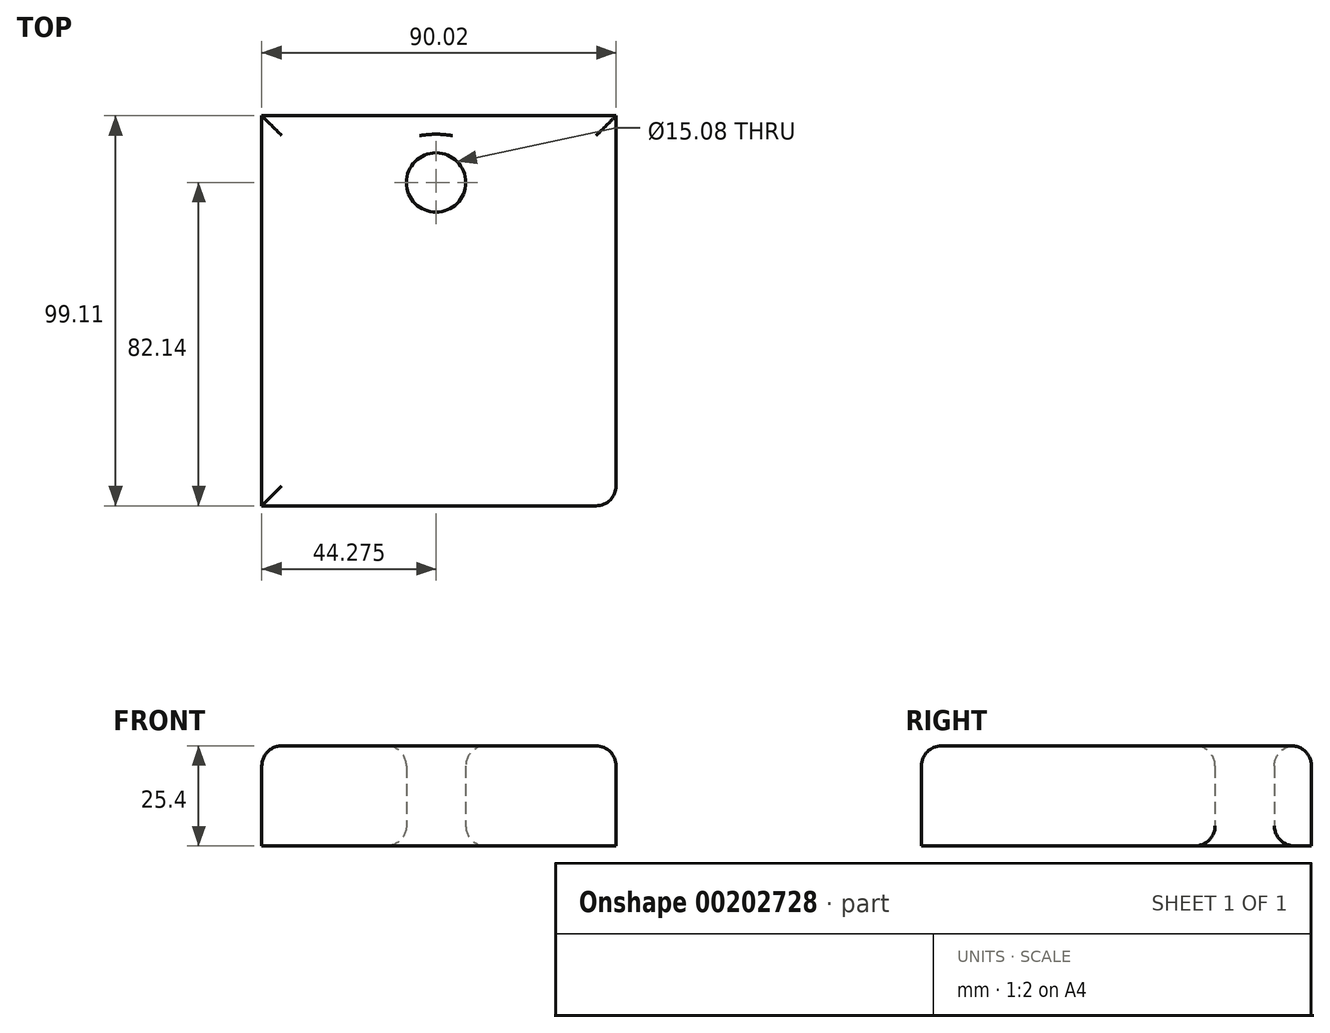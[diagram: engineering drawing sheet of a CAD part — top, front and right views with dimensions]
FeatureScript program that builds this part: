
annotation { "Feature Type Name" : "Feature", "Feature Type Description" : "" }
export const myFeature = defineFeature(function(context is Context, id is Id, definition is map)
    precondition{}
    {
        {
            var Q0;
            Q0=qCreatedBy(makeId("Top.planeOp"),FACE);
            var sketch = newSketch(context, id + "F0", { "sketchPlane" : qUnion([Q0])});
            skLineSegment(sketch, "E0.bottom", {"start": v(-44.12, 51.7) * mm, "end": v(45.9, 51.7) * mm});
            skLineSegment(sketch, "E0.top", {"start": v(-44.12, -47.41) * mm, "end": v(45.9, -47.41) * mm});
            skLineSegment(sketch, "E0.left", {"start": v(-44.12, 51.7) * mm, "end": v(-44.12, -47.41) * mm});
            skLineSegment(sketch, "E0.right", {"start": v(45.9, 51.7) * mm, "end": v(45.9, -47.41) * mm});
            skLineSegment(sketch, "E1", {"start": v(0, 51.7) * mm, "end": v(0.89, -45.83) * mm});
            skPoint(sketch, "E1.endSnap0", {"position": v(0.89, -47.41) * mm});
            skLineSegment(sketch, "E2", {"start": v(0.89, -45.83) * mm, "end": v(0.89, -47.41) * mm});
            skCircle(sketch, "E3", {"center": v(0.15, 34.73) * mm, "radius": 7.54 * mm});
            skSolve(sketch);
        }
        {
            var Q0;
            Q0 = qSketchRegion(id + "F0", true);
            extrude(context, id + "F1", {"entities" : qUnion([Q0]), "depth" : 25.4 * mm});
        }
        {
            var Q0;
            Q0=makeQuery(id+"F1.opExtrude","CAP_EDGE",EDGE,{"disambiguationData":[OSD([sQuery(id+"F0.wireOp",EDGE,"E0.top")])],"isStart":false});
            var Q1;
            Q1=makeQuery(id+"F1.opExtrude","CAP_EDGE",EDGE,{"disambiguationData":[OSD([sQuery(id+"F0.wireOp",EDGE,"E0.right")])],"isStart":false});
            var Q2;
            Q2=makeQuery(id+"F1.opExtrude","SWEPT_EDGE",EDGE,{"disambiguationData":[OSD([sQuery(id+"F0.wireOp",EDGE,"E0.top"),sQuery(id+"F0.wireOp",EDGE,"E0.right")])]});
            var Q3;
            Q3=makeQuery(id+"F1.opExtrude","CAP_EDGE",EDGE,{"disambiguationData":[OSD([sQuery(id+"F0.wireOp",EDGE,"E0.bottom")])],"isStart":false});
            var Q4;
            Q4=makeQuery(id+"F1.opExtrude","CAP_FACE",FACE,{"disambiguationData":[OSD([sQuery(id+"F0.wireOp",EDGE,"E0.bottom"),sQuery(id+"F0.wireOp",EDGE,"E0.top"),sQuery(id+"F0.wireOp",EDGE,"E0.left"),sQuery(id+"F0.wireOp",EDGE,"E0.right"),sQuery(id+"F0.wireOp",EDGE,"E3")])],"isStart":false});
            var Q5;
            Q5=makeQuery(id+"F1.opExtrude","SWEPT_FACE",FACE,{"disambiguationData":[OSD([sQuery(id+"F0.wireOp",EDGE,"E3")])]});
            fillet(context, id + "F2", {"entities" : qUnion([Q0, Q1, Q2, Q3, Q4, Q5]), "radius" : 5.08 * mm, "tangentPropagation" : true, "allowEdgeOverflow" : false});
        }
    });
